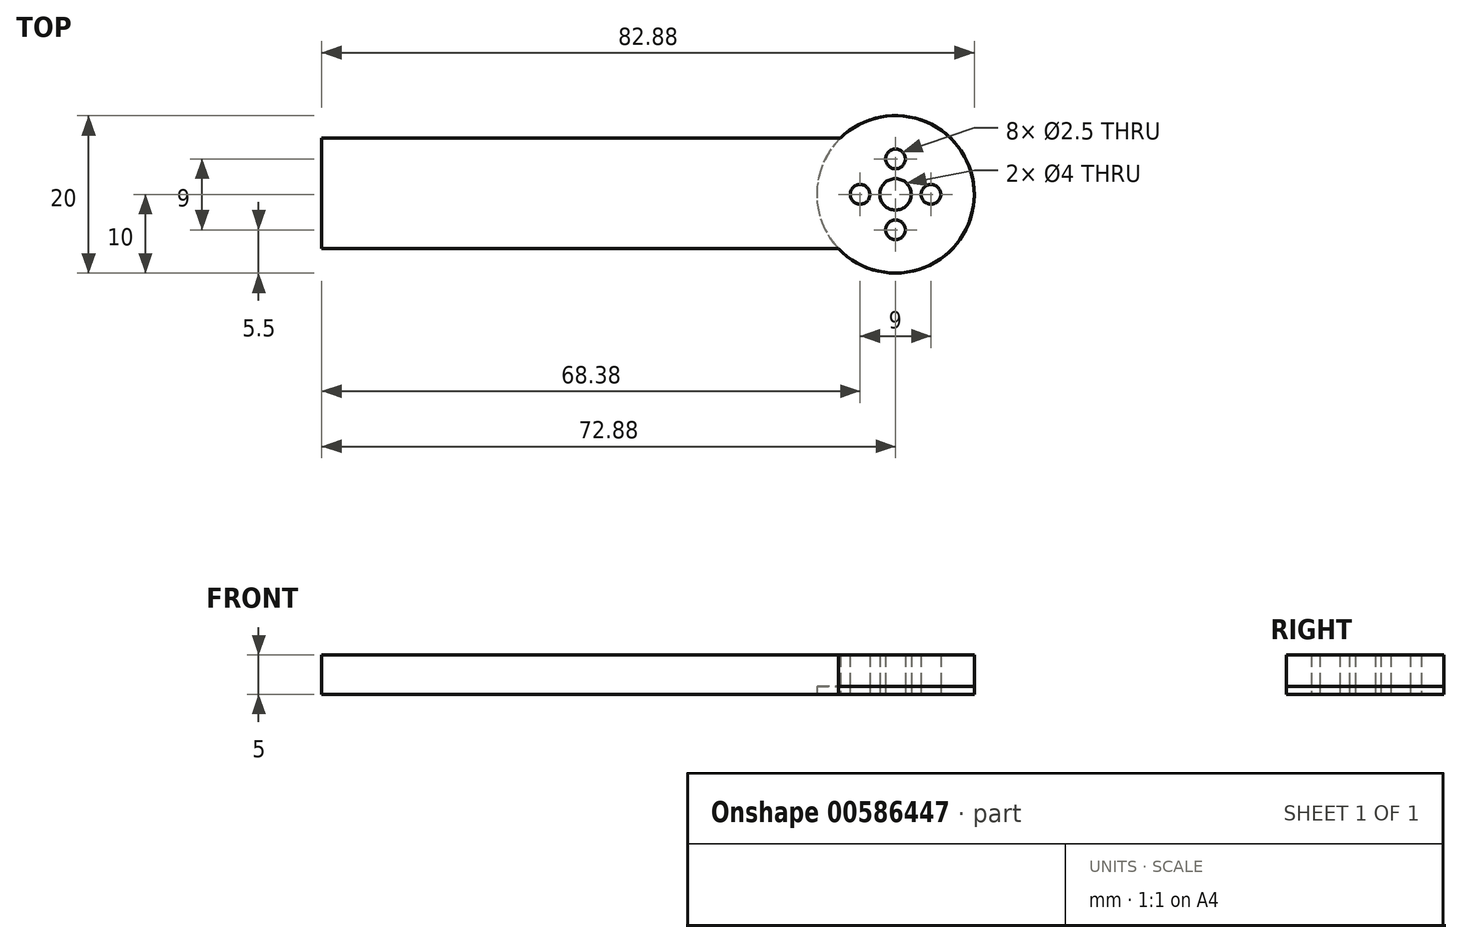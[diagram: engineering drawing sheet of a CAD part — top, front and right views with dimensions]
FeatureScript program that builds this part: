
annotation { "Feature Type Name" : "Feature", "Feature Type Description" : "" }
export const myFeature = defineFeature(function(context is Context, id is Id, definition is map)
    precondition{}
    {
        {
            var Q0;
            Q0=qCreatedBy(makeId("Top.planeOp"),FACE);
            var sketch = newSketch(context, id + "F0", { "sketchPlane" : qUnion([Q0])});
            skLineSegment(sketch, "E0", {"start": v(80, 42.87) * mm, "end": v(80, -37.42) * mm, "construction": true});
            skLineSegment(sketch, "E1", {"start": v(-29.08, 0) * mm, "end": v(65.62, 0) * mm, "construction": true});
            skCircle(sketch, "E2", {"center": v(80, 0) * mm, "radius": 7 * mm, "construction": true});
            skCircle(sketch, "E3", {"center": v(80, 0) * mm, "radius": 4.5 * mm, "construction": true});
            skCircle(sketch, "E4", {"center": v(80, 4.5) * mm, "radius": 1.25 * mm});
            skCircle(sketch, "E5", {"center": v(84.5, 0) * mm, "radius": 1.25 * mm});
            skCircle(sketch, "E6", {"center": v(80, -4.5) * mm, "radius": 1.25 * mm});
            skCircle(sketch, "E7", {"center": v(75.5, 0) * mm, "radius": 1.25 * mm});
            skCircle(sketch, "E8", {"center": v(80, 0) * mm, "radius": 2 * mm});
            skCircle(sketch, "E9", {"center": v(80, 0) * mm, "radius": 10 * mm});
            skArc(sketch, "E10", {"start": v(72.74, -6.88) * mm, "mid": v(90, -0.17) * mm, "end": v(72.98, 7.12) * mm});
            skLineSegment(sketch, "E11.trimOffspring", {"start": v(0, -6.88) * mm, "end": v(72.74, -6.88) * mm});
            skPoint(sketch, "E12.center", {"position": v(-6.47, -7.83) * mm});
            skLineSegment(sketch, "E13", {"start": v(72.98, 7.12) * mm, "end": v(0, 7.12) * mm});
            skPoint(sketch, "E14.1.0", {"position": v(8.08, -6.47) * mm});
            skArc(sketch, "E14.1.1", {"start": v(7.12, 72.74) * mm, "mid": v(0.42, 90) * mm, "end": v(-6.88, 72.98) * mm});
            skCircle(sketch, "E14.1.2", {"center": v(0.25, 80) * mm, "radius": 7 * mm, "construction": true});
            skLineSegment(sketch, "E14.1.3", {"start": v(7.12, 0) * mm, "end": v(7.12, 72.74) * mm});
            skCircle(sketch, "E14.1.4", {"center": v(0.25, 80) * mm, "radius": 4.5 * mm, "construction": true});
            skCircle(sketch, "E14.1.5", {"center": v(0.25, 80) * mm, "radius": 10 * mm});
            skLineSegment(sketch, "E14.1.6", {"start": v(-6.88, 72.98) * mm, "end": v(-6.88, 0) * mm});
            skCircle(sketch, "E14.1.7", {"center": v(0.25, 80) * mm, "radius": 2 * mm});
            skCircle(sketch, "E14.1.8", {"center": v(0.25, 75.5) * mm, "radius": 1.25 * mm});
            skCircle(sketch, "E14.1.9", {"center": v(0.25, 84.5) * mm, "radius": 1.25 * mm});
            skCircle(sketch, "E14.1.10", {"center": v(-4.25, 80) * mm, "radius": 1.25 * mm});
            skCircle(sketch, "E14.1.11", {"center": v(4.75, 80) * mm, "radius": 1.25 * mm});
            skPoint(sketch, "E14.2.0", {"position": v(6.72, 8.08) * mm});
            skArc(sketch, "E14.2.1", {"start": v(-72.5, 7.12) * mm, "mid": v(-89.75, 0.42) * mm, "end": v(-72.73, -6.88) * mm});
            skCircle(sketch, "E14.2.2", {"center": v(-79.75, 0.25) * mm, "radius": 7 * mm, "construction": true});
            skLineSegment(sketch, "E14.2.3", {"start": v(0.25, 7.12) * mm, "end": v(-72.5, 7.12) * mm});
            skCircle(sketch, "E14.2.4", {"center": v(-79.75, 0.25) * mm, "radius": 4.5 * mm, "construction": true});
            skCircle(sketch, "E14.2.5", {"center": v(-79.75, 0.25) * mm, "radius": 10 * mm});
            skLineSegment(sketch, "E14.2.6", {"start": v(-72.73, -6.88) * mm, "end": v(0.25, -6.88) * mm});
            skCircle(sketch, "E14.2.7", {"center": v(-79.75, 0.25) * mm, "radius": 2 * mm});
            skCircle(sketch, "E14.2.8", {"center": v(-75.25, 0.25) * mm, "radius": 1.25 * mm});
            skCircle(sketch, "E14.2.9", {"center": v(-84.25, 0.25) * mm, "radius": 1.25 * mm});
            skCircle(sketch, "E14.2.10", {"center": v(-79.75, -4.25) * mm, "radius": 1.25 * mm});
            skCircle(sketch, "E14.2.11", {"center": v(-79.75, 4.75) * mm, "radius": 1.25 * mm});
            skPoint(sketch, "E14.3.0", {"position": v(-7.83, 6.72) * mm});
            skArc(sketch, "E14.3.1", {"start": v(-6.88, -72.5) * mm, "mid": v(-0.17, -89.75) * mm, "end": v(7.12, -72.73) * mm});
            skCircle(sketch, "E14.3.2", {"center": v(0, -79.75) * mm, "radius": 7 * mm, "construction": true});
            skLineSegment(sketch, "E14.3.3", {"start": v(-6.88, 0.25) * mm, "end": v(-6.88, -72.5) * mm});
            skCircle(sketch, "E14.3.4", {"center": v(0, -79.75) * mm, "radius": 4.5 * mm, "construction": true});
            skCircle(sketch, "E14.3.5", {"center": v(0, -79.75) * mm, "radius": 10 * mm});
            skLineSegment(sketch, "E14.3.6", {"start": v(7.12, -72.73) * mm, "end": v(7.12, 0.25) * mm});
            skCircle(sketch, "E14.3.7", {"center": v(0, -79.75) * mm, "radius": 2 * mm});
            skCircle(sketch, "E14.3.8", {"center": v(0, -75.25) * mm, "radius": 1.25 * mm});
            skCircle(sketch, "E14.3.9", {"center": v(0, -84.25) * mm, "radius": 1.25 * mm});
            skCircle(sketch, "E14.3.10", {"center": v(4.5, -79.75) * mm, "radius": 1.25 * mm});
            skCircle(sketch, "E14.3.11", {"center": v(-4.5, -79.75) * mm, "radius": 1.25 * mm});
            skPoint(sketch, "E14.center", {"position": v(0.12, 0.12) * mm});
            skSolve(sketch);
        }
        {
            var Q0;
            Q0=makeQuery(id+"F0.imprint","IMPRINT",FACE,{"disambiguationData":[TD([[makeQuery(id+"F0.imprint","IMPRINT",EDGE,{"derivedFrom":sQuery(id+"F0.wireOp",EDGE,"E9")}),-1.0]])]});
            var Q1;
            {var subQ7=sQuery(id+"F0.wireOp",EDGE,"E14.2.3");var subQ8=makeQuery(id+"F0.imprint","IMPRINT",VERTEX,{"derivedFrom":subQ7});Q1=makeQuery(id+"F0.imprint","IMPRINT",FACE,{"disambiguationData":[TD([[makeQuery(id+"F0.imprint","IMPRINT",EDGE,{"disambiguationData":[TD([[subQ8,1.0]])],"derivedFrom":subQ7}),-1.0]])]});}
            var Q2;
            {var subQ7=sQuery(id+"F0.wireOp",EDGE,"E14.2.3");var subQ8=makeQuery(id+"F0.imprint","IMPRINT",VERTEX,{"derivedFrom":subQ7});Q2=makeQuery(id+"F0.imprint","IMPRINT",FACE,{"disambiguationData":[TD([[makeQuery(id+"F0.imprint","IMPRINT",EDGE,{"disambiguationData":[TD([[subQ8,1.0]])],"derivedFrom":subQ7}),1.0]])]});}
            var Q3;
            {var subQ3=sQuery(id+"F0.wireOp",EDGE,"E14.3.3");var subQ10=makeQuery(id+"F0.imprint","IMPRINT",VERTEX,{"derivedFrom":subQ3});Q3=makeQuery(id+"F0.imprint","IMPRINT",FACE,{"disambiguationData":[TD([[makeQuery(id+"F0.imprint","IMPRINT",EDGE,{"disambiguationData":[TD([[subQ10,1.0]])],"derivedFrom":subQ3}),-1.0]])]});}
            var Q4;
            {var subQ0=sQuery(id+"F0.wireOp",EDGE,"E14.2.6");var subQ3=makeQuery(id+"F0.imprint","IMPRINT",VERTEX,{"derivedFrom":subQ0});Q4=makeQuery(id+"F0.imprint","IMPRINT",FACE,{"disambiguationData":[TD([[makeQuery(id+"F0.imprint","IMPRINT",EDGE,{"disambiguationData":[TD([[subQ3,1.0]])],"derivedFrom":subQ0}),-1.0]])]});}
            var Q5;
            Q5=makeQuery(id+"F0.imprint","IMPRINT",FACE,{"disambiguationData":[TD([[makeQuery(id+"F0.imprint","IMPRINT",EDGE,{"derivedFrom":sQuery(id+"F0.wireOp",EDGE,"E4")}),-1.0]])]});
            extrude(context, id + "F1", {"entities" : qUnion([Q0, Q1, Q2, Q3, Q4, Q5]), "depth" : 5 * mm, "offsetDistance" : 25 * mm});
        }
        {
            var Q0;
            Q0=makeQuery(id+"F0.imprint","IMPRINT",FACE,{"disambiguationData":[TD([[makeQuery(id+"F0.imprint","IMPRINT",EDGE,{"derivedFrom":sQuery(id+"F0.wireOp",EDGE,"E4")}),-1.0]])]});
            extrude(context, id + "F2", {"entities" : qUnion([Q0]), "depth" : 1 * mm, "offsetDistance" : 25 * mm});
        }
    });
